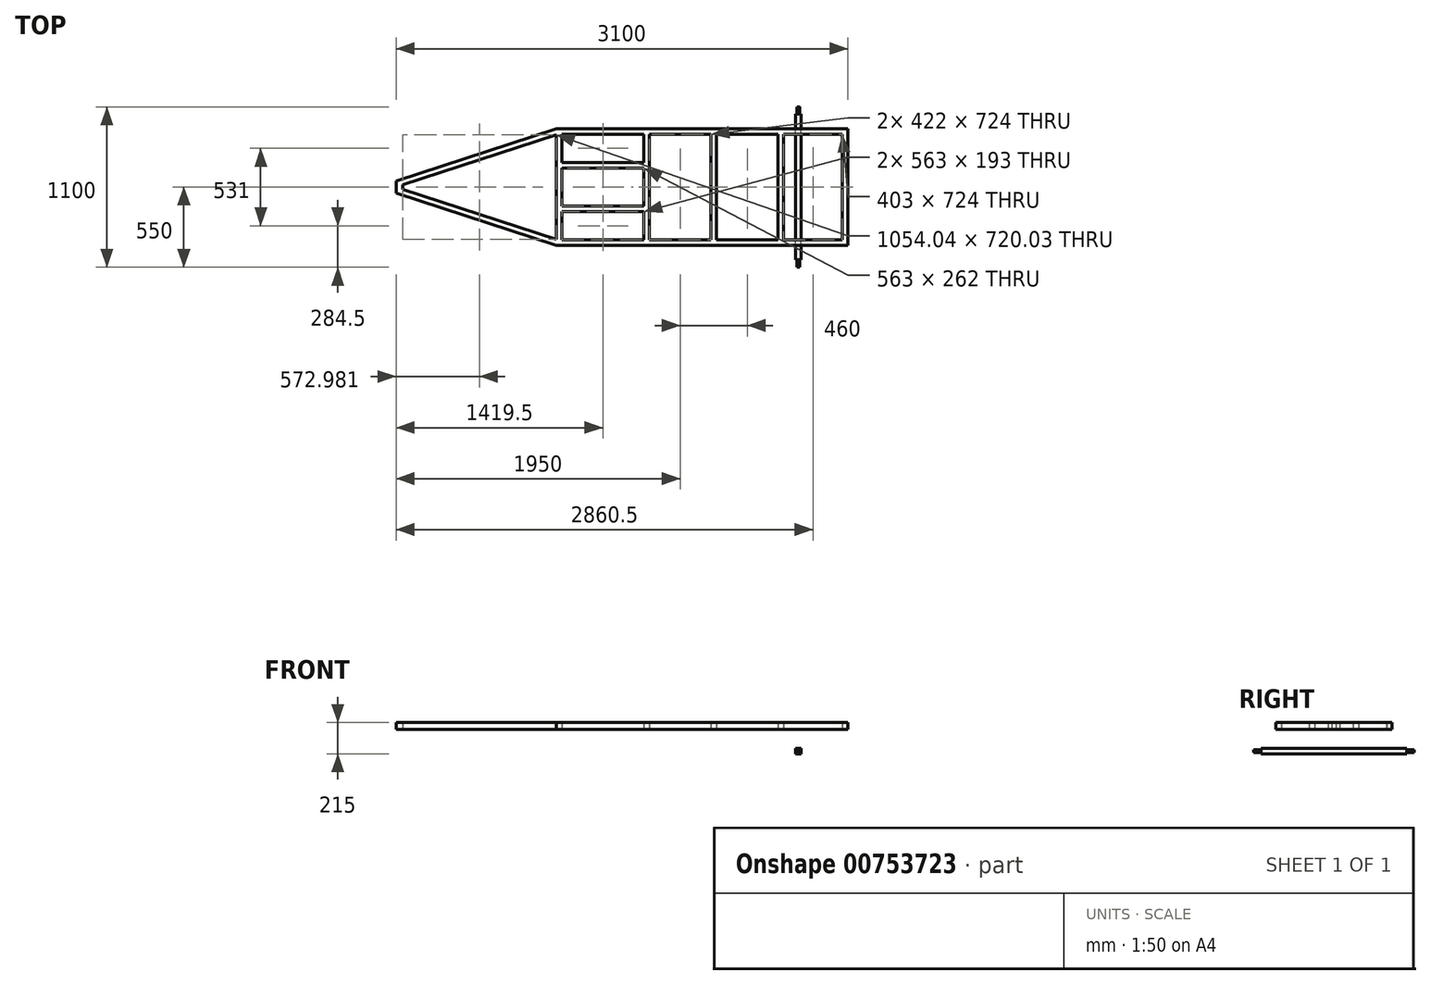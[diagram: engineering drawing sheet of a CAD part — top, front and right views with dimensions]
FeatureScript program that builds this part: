
annotation { "Feature Type Name" : "Feature", "Feature Type Description" : "" }
export const myFeature = defineFeature(function(context is Context, id is Id, definition is map)
    precondition{}
    {
        {
            var Q0;
            Q0=qCreatedBy(makeId("Top.planeOp"),FACE);
            var sketch = newSketch(context, id + "F0", { "sketchPlane" : qUnion([Q0])});
            skLineSegment(sketch, "E0.bottom", {"start": v(1000, 400) * mm, "end": v(-1000, 400) * mm});
            skLineSegment(sketch, "E0.top", {"start": v(1000, -400) * mm, "end": v(-1000, -400) * mm});
            skLineSegment(sketch, "E0.left", {"start": v(1000, 400) * mm, "end": v(1000, -400) * mm});
            skLineSegment(sketch, "E0.right", {"start": v(-1000, 360.02) * mm, "end": v(-1000, -360.02) * mm});
            skPoint(sketch, "E0.middle", {"position": v(0, 0) * mm});
            skLineSegment(sketch, "E1.0", {"start": v(962, 362) * mm, "end": v(559, 362) * mm});
            skLineSegment(sketch, "E1.1", {"start": v(962, 362) * mm, "end": v(962, -362) * mm});
            skLineSegment(sketch, "E1.2", {"start": v(962, -362) * mm, "end": v(559, -362) * mm});
            skLineSegment(sketch, "E1.3", {"start": v(-962, 362) * mm, "end": v(-962, 169) * mm});
            skLineSegment(sketch, "E2.left", {"start": v(-361, 362) * mm, "end": v(-361, -362) * mm});
            skLineSegment(sketch, "E2.right", {"start": v(-399, 362) * mm, "end": v(-399, 169) * mm});
            skLineSegment(sketch, "E3.left", {"start": v(61, 362) * mm, "end": v(61, -362) * mm});
            skLineSegment(sketch, "E3.right", {"start": v(99, 362) * mm, "end": v(99, -362) * mm});
            skLineSegment(sketch, "E4.left", {"start": v(521, 362) * mm, "end": v(521, -362) * mm});
            skLineSegment(sketch, "E4.right", {"start": v(559, 362) * mm, "end": v(559, -362) * mm});
            skLineSegment(sketch, "E5.trimOffspring", {"start": v(-399, 362) * mm, "end": v(-962, 362) * mm});
            skLineSegment(sketch, "E6.trimOffspring", {"start": v(61, 362) * mm, "end": v(-361, 362) * mm});
            skLineSegment(sketch, "E7.trimOffspring", {"start": v(61, -362) * mm, "end": v(-361, -362) * mm});
            skLineSegment(sketch, "E8.trimOffspring", {"start": v(521, -362) * mm, "end": v(99, -362) * mm});
            skLineSegment(sketch, "E9.trimOffspring", {"start": v(521, 362) * mm, "end": v(99, 362) * mm});
            skPoint(sketch, "E10.orphan", {"position": v(-1000, 559.81) * mm});
            skLineSegment(sketch, "E11", {"start": v(-2100, -40) * mm, "end": v(-2100, 40) * mm});
            skLineSegment(sketch, "E12", {"start": v(-1000, 400) * mm, "end": v(-2100, 40) * mm});
            skLineSegment(sketch, "E13", {"start": v(-1000, -400) * mm, "end": v(-2100, -40) * mm});
            skLineSegment(sketch, "E14.0", {"start": v(-1000, -360.02) * mm, "end": v(-2054.04, -15.06) * mm});
            skLineSegment(sketch, "E15.0", {"start": v(-1000, 360.02) * mm, "end": v(-2054.04, 15.06) * mm});
            skLineSegment(sketch, "E16.0", {"start": v(-2054.04, -15.06) * mm, "end": v(-2054.04, 15.06) * mm});
            skLineSegment(sketch, "E17.bottom", {"start": v(-962, 131) * mm, "end": v(-399, 131) * mm});
            skLineSegment(sketch, "E17.top", {"start": v(-962, 169) * mm, "end": v(-399, 169) * mm});
            skLineSegment(sketch, "E18.bottom", {"start": v(-962, -169) * mm, "end": v(-399, -169) * mm});
            skLineSegment(sketch, "E18.top", {"start": v(-962, -131) * mm, "end": v(-399, -131) * mm});
            skLineSegment(sketch, "E19", {"start": v(-380, -431.81) * mm, "end": v(-380, 517.63) * mm, "construction": true});
            skLineSegment(sketch, "E20", {"start": v(80, -431.81) * mm, "end": v(80, 517.63) * mm, "construction": true});
            skLineSegment(sketch, "E21", {"start": v(540, -431.81) * mm, "end": v(540, 517.63) * mm, "construction": true});
            skLineSegment(sketch, "E22", {"start": v(1069.9, 150) * mm, "end": v(-1087.37, 150) * mm, "construction": true});
            skLineSegment(sketch, "E23", {"start": v(1069.9, -150) * mm, "end": v(-1087.37, -150) * mm, "construction": true});
            skPoint(sketch, "E24.orphan", {"position": v(-380, 362) * mm});
            skLineSegment(sketch, "E25.trimOffspring", {"start": v(-399, 131) * mm, "end": v(-399, -131) * mm});
            skLineSegment(sketch, "E26.trimOffspring", {"start": v(-399, -169) * mm, "end": v(-399, -362) * mm});
            skLineSegment(sketch, "E27.trimOffspring", {"start": v(-380, -169) * mm, "end": v(-379.96, -169) * mm});
            skLineSegment(sketch, "E28.trimOffspring", {"start": v(-962, 131) * mm, "end": v(-962, -131) * mm});
            skLineSegment(sketch, "E29.trimOffspring", {"start": v(-962, -169) * mm, "end": v(-962, -362) * mm});
            skLineSegment(sketch, "E30.trimOffspring", {"start": v(-399, -362) * mm, "end": v(-962, -362) * mm});
            skSolve(sketch);
        }
        {
            var Q0;
            Q0=makeQuery(id+"F0.imprint","IMPRINT",FACE,{"disambiguationData":[TD([[makeQuery(id+"F0.imprint","IMPRINT",EDGE,{"derivedFrom":sQuery(id+"F0.wireOp",EDGE,"E0.bottom")}),1.0]])]});
            var Q1;
            Q1=makeQuery(id+"F0.imprint","IMPRINT",FACE,{"disambiguationData":[TD([[makeQuery(id+"F0.imprint","IMPRINT",EDGE,{"derivedFrom":sQuery(id+"F0.wireOp",EDGE,"E18.bottom")}),1.0]])]});
            var Q2;
            Q2=makeQuery(id+"F0.imprint","IMPRINT",FACE,{"disambiguationData":[TD([[makeQuery(id+"F0.imprint","IMPRINT",EDGE,{"derivedFrom":sQuery(id+"F0.wireOp",EDGE,"E17.bottom")}),1.0]])]});
            extrude(context, id + "F1", {"entities" : qUnion([Q0, Q1, Q2]), "depth" : 45 * mm, "offsetDistance" : 25 * mm});
        }
        {
            var Q0;
            Q0=qCreatedBy(makeId("Front.planeOp"),FACE);
            var sketch = newSketch(context, id + "F2", { "sketchPlane" : qUnion([Q0])});
            skLineSegment(sketch, "E31.bottom", {"start": v(640, -130) * mm, "end": v(680, -130) * mm});
            skLineSegment(sketch, "E31.top", {"start": v(640, -170) * mm, "end": v(680, -170) * mm});
            skLineSegment(sketch, "E31.left", {"start": v(640, -130) * mm, "end": v(640, -170) * mm});
            skLineSegment(sketch, "E31.right", {"start": v(680, -130) * mm, "end": v(680, -170) * mm});
            skCircle(sketch, "E32", {"center": v(660, -150) * mm, "radius": 9.44 * mm});
            skPoint(sketch, "E32.centerSnap0", {"position": v(640, -150) * mm});
            skSolve(sketch);
        }
        {
            var Q0;
            Q0=makeQuery(id+"F2.imprint","IMPRINT",FACE,{"disambiguationData":[TD([[makeQuery(id+"F2.imprint","IMPRINT",EDGE,{"derivedFrom":sQuery(id+"F2.wireOp",EDGE,"E31.bottom")}),-1.0]])]});
            extrude(context, id + "F3", {"entities" : qUnion([Q0]), "endBound" : BoundingType.SYMMETRIC, "depth" : 1000 * mm, "offsetDistance" : 25 * mm});
        }
        {
            var Q0;
            Q0=makeQuery(id+"F2.imprint","IMPRINT",FACE,{"disambiguationData":[TD([[makeQuery(id+"F2.imprint","IMPRINT",EDGE,{"derivedFrom":sQuery(id+"F2.wireOp",EDGE,"E32")}),1.0]])]});
            extrude(context, id + "F4", {"entities" : qUnion([Q0]), "operationType" : NewBodyOperationType.ADD, "endBound" : BoundingType.SYMMETRIC, "depth" : 1100 * mm, "offsetDistance" : 25 * mm});
        }
    });
